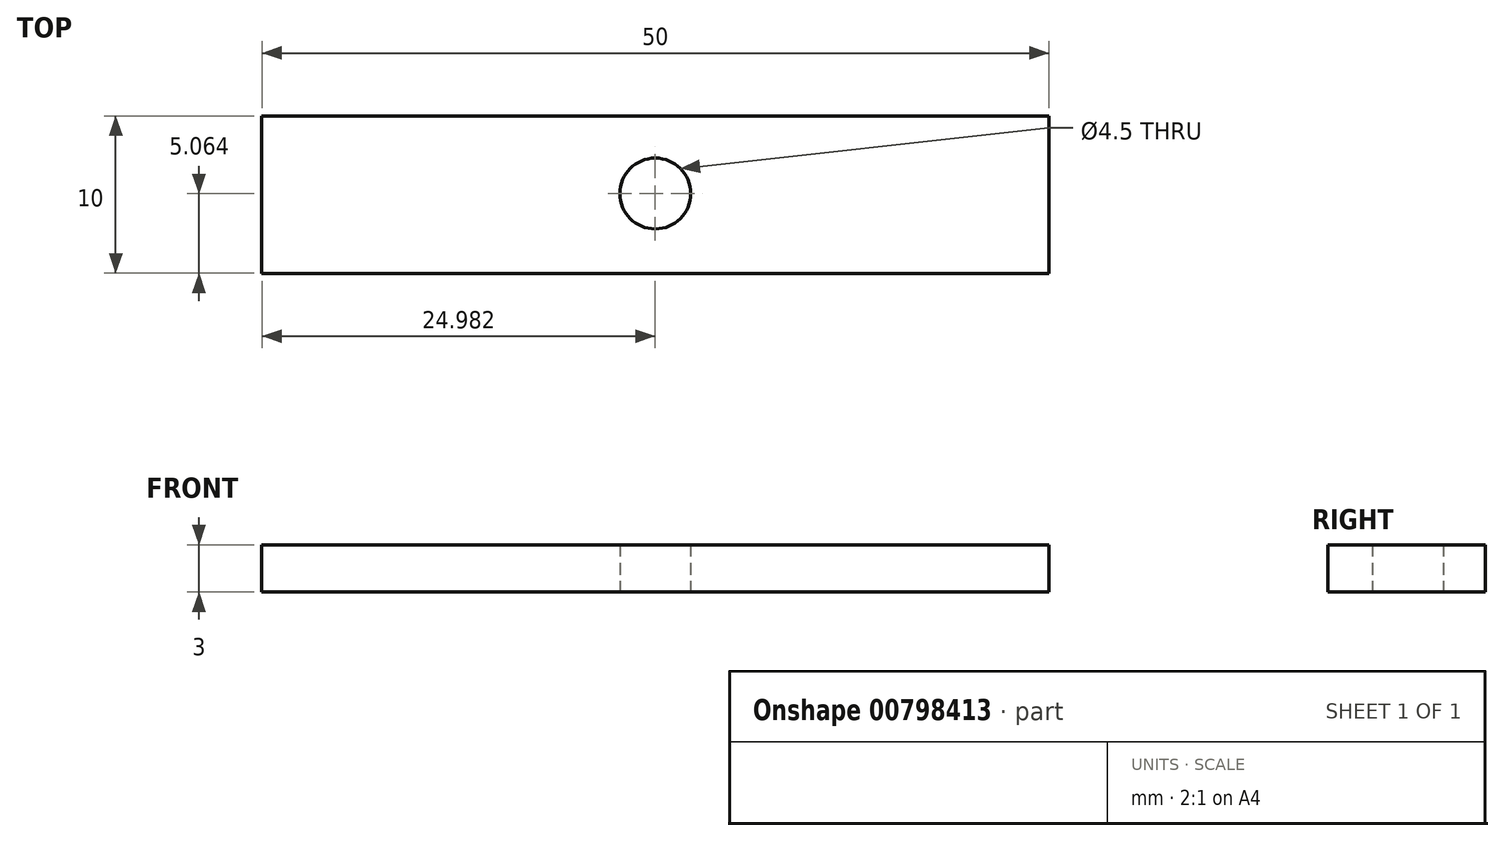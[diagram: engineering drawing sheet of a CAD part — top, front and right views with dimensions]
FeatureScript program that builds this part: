
annotation { "Feature Type Name" : "Feature", "Feature Type Description" : "" }
export const myFeature = defineFeature(function(context is Context, id is Id, definition is map)
    precondition{}
    {
        {
            var Q0;
            Q0=qCreatedBy(makeId("Top.planeOp"),FACE);
            var sketch = newSketch(context, id + "F0", { "sketchPlane" : qUnion([Q0])});
            skLineSegment(sketch, "E0.bottom", {"start": v(5.4, 4.87) * mm, "end": v(55.4, 4.87) * mm});
            skLineSegment(sketch, "E0.top", {"start": v(5.4, -5.13) * mm, "end": v(55.4, -5.13) * mm});
            skLineSegment(sketch, "E0.left", {"start": v(5.4, 4.87) * mm, "end": v(5.4, -5.13) * mm});
            skLineSegment(sketch, "E0.right", {"start": v(55.4, 4.87) * mm, "end": v(55.4, -5.13) * mm});
            skLineSegment(sketch, "E1", {"start": v(5.4, -0.13) * mm, "end": v(55.4, 0) * mm, "construction": true});
            skLineSegment(sketch, "E2", {"start": v(30.4, -5.13) * mm, "end": v(30.37, 4.87) * mm, "construction": true});
            skPoint(sketch, "E3", {"position": v(30.38, -0.07) * mm});
            skSolve(sketch);
        }
        {
            var Q0;
            Q0=makeQuery(id+"F0.imprint","IMPRINT",FACE,{"disambiguationData":[TD([[makeQuery(id+"F0.imprint","IMPRINT",EDGE,{"derivedFrom":sQuery(id+"F0.wireOp",EDGE,"E0.bottom")}),-1.0]])]});
            extrude(context, id + "F1", {"entities" : qUnion([Q0]), "depth" : 3 * mm, "offsetDistance" : 25 * mm});
        }
        {
            var Q0;
            Q0=sQuery(id+"F0.wireOp",VERTEX,"E3");
            var Q1;
            Q1=makeQuery(id+"F1.opExtrude","SWEPT_BODY",BODY,{"disambiguationData":[OSD([sQuery(id+"F0.wireOp",EDGE,"E0.bottom"),sQuery(id+"F0.wireOp",EDGE,"E0.top"),sQuery(id+"F0.wireOp",EDGE,"E0.left"),sQuery(id+"F0.wireOp",EDGE,"E0.right")])]});
            hole(context, id + "F2", {"style" : HoleStyle.SIMPLE, "endStyle" : HoleEndStyle.THROUGH, "oppositeDirection" : true, "standardTappedOrClearance" : lookupTablePath({ "fit" : "Normal", "standard" : "ISO", "size" : "M4", "type" : "Clearance" }), "standardBlindInLast" : lookupTablePath({ "fit" : "Normal", "standard" : "ISO", "engagement" : "75%", "pitch" : "0.7 mm", "size" : "M4", "type" : "Clearance & tapped" }), "holeDiameter" : 4.5 * mm, "majorDiameter" : 5 * mm, "tappedDepth" : 12 * mm, "tapClearance" : 3, "locations" : qUnion([Q0]), "scope" : qUnion([Q1])});
        }
    });
